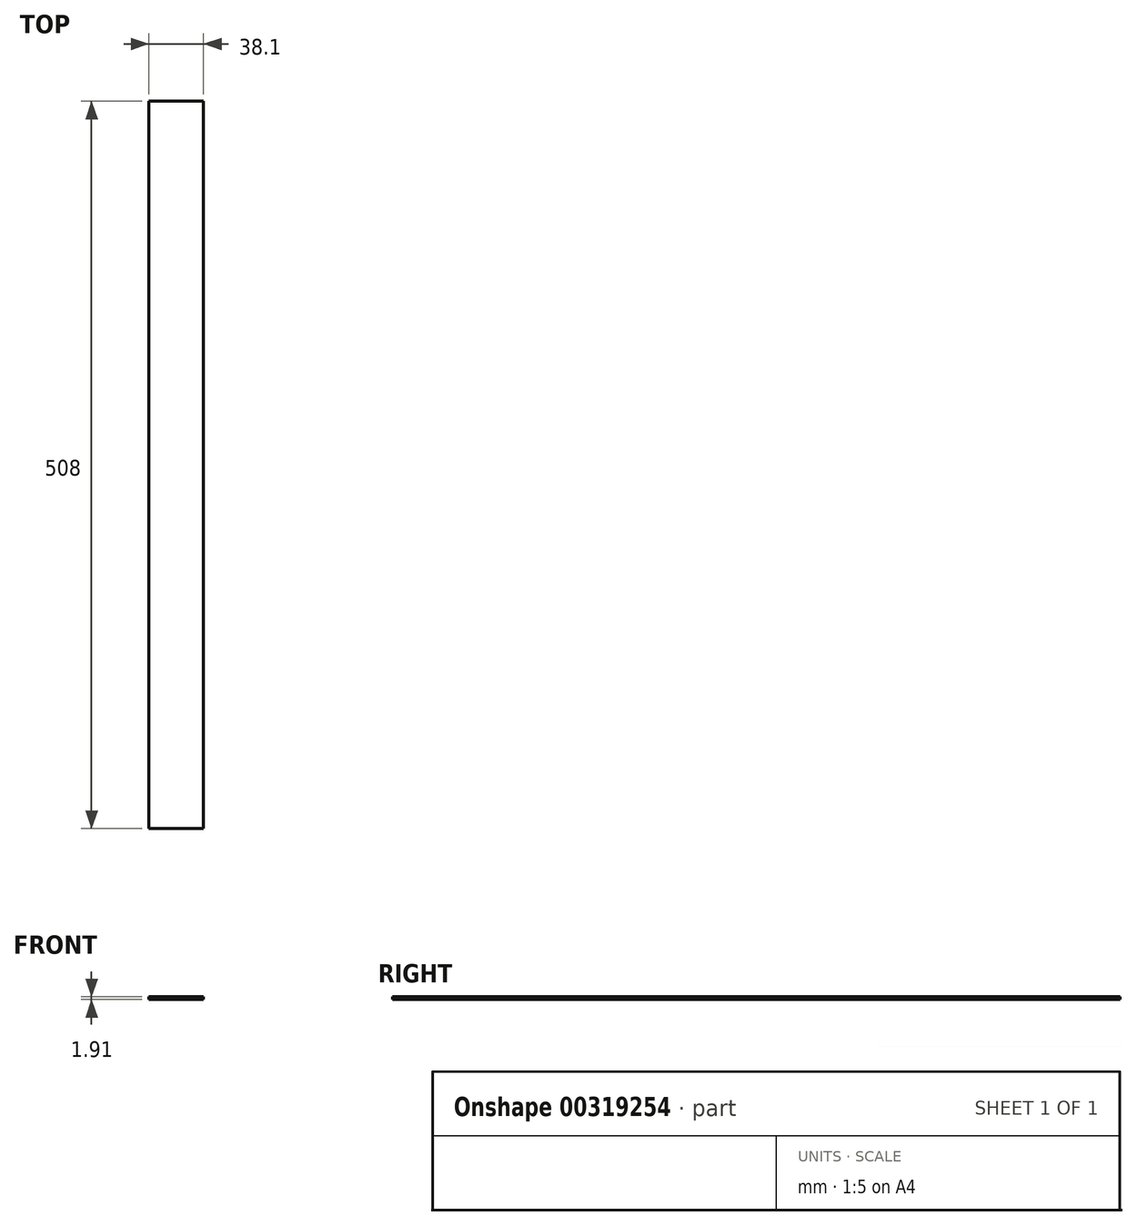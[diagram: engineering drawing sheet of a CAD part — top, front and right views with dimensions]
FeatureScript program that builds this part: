
annotation { "Feature Type Name" : "Feature", "Feature Type Description" : "" }
export const myFeature = defineFeature(function(context is Context, id is Id, definition is map)
    precondition{}
    {
        {
            var Q0;
            Q0=qCreatedBy(makeId("Front.planeOp"),FACE);
            var sketch = newSketch(context, id + "F0", { "sketchPlane" : qUnion([Q0])});
            skLineSegment(sketch, "E0", {"start": v(0, 0) * mm, "end": v(38.1, 0) * mm});
            skLineSegment(sketch, "E1", {"start": v(38.1, 0) * mm, "end": v(38.1, -1.9) * mm});
            skLineSegment(sketch, "E2", {"start": v(38.1, -1.9) * mm, "end": v(0, -1.9) * mm});
            skLineSegment(sketch, "E3", {"start": v(0, -1.9) * mm, "end": v(0, 0) * mm});
            skSolve(sketch);
        }
        {
            var Q0;
            Q0=makeQuery(id+"F0.imprint","IMPRINT",FACE,{"disambiguationData":[TD([[makeQuery(id+"F0.imprint","IMPRINT",EDGE,{"derivedFrom":sQuery(id+"F0.wireOp",EDGE,"E0")}),-1.0]])]});
            extrude(context, id + "F1", {"entities" : qUnion([Q0]), "oppositeDirection" : true, "depth" : 508 * mm});
        }
    });
